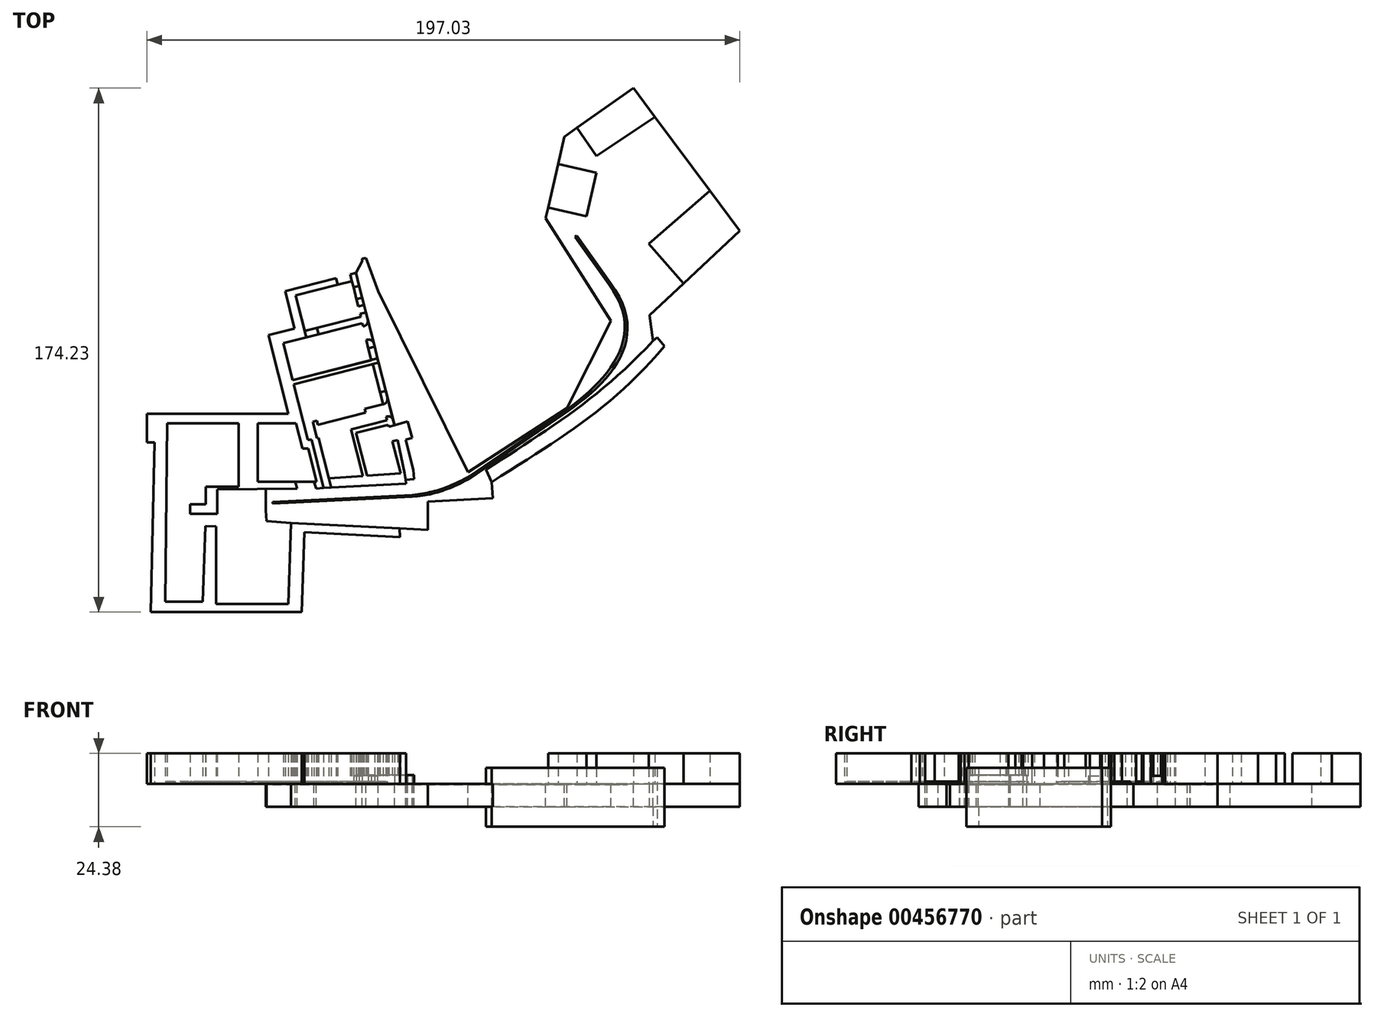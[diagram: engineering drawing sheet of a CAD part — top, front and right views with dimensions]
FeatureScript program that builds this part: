
annotation { "Feature Type Name" : "Feature", "Feature Type Description" : "" }
export const myFeature = defineFeature(function(context is Context, id is Id, definition is map)
    precondition{}
    {
        {
            var Q0;
            Q0=qCreatedBy(makeId("Top.planeOp"),FACE);
            var sketch = newSketch(context, id + "F0", { "sketchPlane" : qUnion([Q0])});
            skLineSegment(sketch, "E0", {"start": v(-16.8, 59.4) * mm, "end": v(-12.68, 48.38) * mm});
            skLineSegment(sketch, "E1", {"start": v(-12.68, 48.38) * mm, "end": v(17.13, -11.76) * mm});
            skLineSegment(sketch, "E2", {"start": v(17.13, -11.76) * mm, "end": v(50, 9.46) * mm});
            skLineSegment(sketch, "E3", {"start": v(50, 9.46) * mm, "end": v(64.66, 38.46) * mm});
            skLineSegment(sketch, "E4", {"start": v(64.66, 38.46) * mm, "end": v(42.95, 72.6) * mm});
            skLineSegment(sketch, "E5", {"start": v(50.27, 9.14) * mm, "end": v(17.8, -13.14) * mm});
            skLineSegment(sketch, "E6", {"start": v(-1.42, -19.38) * mm, "end": v(-47.79, -21.76) * mm});
            skLineSegment(sketch, "E7", {"start": v(-33.32, -17.22) * mm, "end": v(-3.46, -15.64) * mm});
            skLineSegment(sketch, "E8", {"start": v(-3.46, -15.64) * mm, "end": v(-3.54, -14.3) * mm});
            skLineSegment(sketch, "E9", {"start": v(-3.54, -14.3) * mm, "end": v(-0.76, -14.12) * mm});
            skLineSegment(sketch, "E10", {"start": v(-0.76, -14.12) * mm, "end": v(-0.95, -11.07) * mm});
            skLineSegment(sketch, "E11", {"start": v(-0.95, -11.07) * mm, "end": v(-3.53, -0.98) * mm});
            skLineSegment(sketch, "E12", {"start": v(-3.53, -0.98) * mm, "end": v(-1.33, -0.41) * mm});
            skLineSegment(sketch, "E13", {"start": v(-1.33, -0.41) * mm, "end": v(-2.86, 5.03) * mm});
            skLineSegment(sketch, "E14", {"start": v(-2.86, 5.03) * mm, "end": v(-7.26, 3.75) * mm});
            skLineSegment(sketch, "E15", {"start": v(-7.26, 3.75) * mm, "end": v(-20.08, 54.46) * mm});
            skFitSpline(sketch, "E16", {"points": [v(63.94, 50.75) * mm, v(50.27, 9.14) * mm], "startDerivative": vector(38.1, -51.9) * mm, "endDerivative": vector(-42.14, -31.36) * mm});
            skFitSpline(sketch, "E17", {"points": [v(17.8, -13.14) * mm, v(-1.42, -19.38) * mm], "startDerivative": vector(-22.13, -11.78) * mm, "endDerivative": vector(-20.75, -1.85) * mm});
            skLineSegment(sketch, "E18", {"start": v(-33.32, -17.22) * mm, "end": v(-34.01, -14.95) * mm});
            skLineSegment(sketch, "E19", {"start": v(-34.01, -14.95) * mm, "end": v(-40.26, -14.95) * mm});
            skLineSegment(sketch, "E20", {"start": v(-40.26, -14.95) * mm, "end": v(-39.68, -17.22) * mm});
            skLineSegment(sketch, "E21", {"start": v(-16.8, 59.4) * mm, "end": v(-18.08, 59.2) * mm});
            skLineSegment(sketch, "E22", {"start": v(-18.08, 59.2) * mm, "end": v(-18.08, 58.33) * mm});
            skLineSegment(sketch, "E23", {"start": v(-18.08, 58.33) * mm, "end": v(-20.08, 54.46) * mm});
            skLineSegment(sketch, "E24", {"start": v(-19.5, 52.18) * mm, "end": v(-40.07, 46.98) * mm});
            skLineSegment(sketch, "E25", {"start": v(-40.07, 46.98) * mm, "end": v(-37.07, 35.13) * mm});
            skLineSegment(sketch, "E26", {"start": v(-37.07, 35.13) * mm, "end": v(-18.4, 39.85) * mm});
            skLineSegment(sketch, "E27", {"start": v(-18.4, 39.85) * mm, "end": v(-18.65, 40.83) * mm});
            skLineSegment(sketch, "E28", {"start": v(-18.65, 40.83) * mm, "end": v(-16.76, 41.3) * mm});
            skLineSegment(sketch, "E29", {"start": v(-17.38, 43.77) * mm, "end": v(-19.28, 43.29) * mm});
            skLineSegment(sketch, "E30", {"start": v(-19.28, 43.29) * mm, "end": v(-21.4, 51.7) * mm});
            skLineSegment(sketch, "E31", {"start": v(-20.88, 49.63) * mm, "end": v(-18.98, 50.11) * mm});
            skLineSegment(sketch, "E32", {"start": v(-19.9, 45.75) * mm, "end": v(-18, 46.22) * mm});
            skLineSegment(sketch, "E33", {"start": v(-17.7, 36.65) * mm, "end": v(-17.98, 37.72) * mm});
            skLineSegment(sketch, "E34", {"start": v(-17.98, 37.72) * mm, "end": v(-44.24, 31.08) * mm});
            skLineSegment(sketch, "E35", {"start": v(-44.24, 31.08) * mm, "end": v(-41.14, 18.82) * mm});
            skLineSegment(sketch, "E36", {"start": v(-41.14, 18.82) * mm, "end": v(-14.94, 25.45) * mm});
            skLineSegment(sketch, "E37", {"start": v(-14.94, 25.45) * mm, "end": v(-16.63, 32.14) * mm});
            skLineSegment(sketch, "E38", {"start": v(-15.93, 29.39) * mm, "end": v(-13.87, 29.9) * mm});
            skLineSegment(sketch, "E39", {"start": v(-14.94, 25.45) * mm, "end": v(-12.88, 25.97) * mm});
            skLineSegment(sketch, "E40", {"start": v(-41.14, 18.82) * mm, "end": v(-40.78, 17.42) * mm});
            skLineSegment(sketch, "E41", {"start": v(-40.78, 17.42) * mm, "end": v(-12.52, 24.57) * mm});
            skLineSegment(sketch, "E42", {"start": v(-12.52, 24.57) * mm, "end": v(-14.44, 24.09) * mm});
            skLineSegment(sketch, "E43", {"start": v(-14.44, 24.09) * mm, "end": v(-9.72, 5.42) * mm});
            skLineSegment(sketch, "E44", {"start": v(-9.72, 5.42) * mm, "end": v(-33.02, -0.47) * mm});
            skLineSegment(sketch, "E45", {"start": v(-33.02, -0.47) * mm, "end": v(-34.4, 4.99) * mm});
            skLineSegment(sketch, "E46", {"start": v(-32.46, -0.33) * mm, "end": v(-29.05, -13.83) * mm});
            skLineSegment(sketch, "E47", {"start": v(-29.05, -13.83) * mm, "end": v(-17.78, -13.1) * mm});
            skLineSegment(sketch, "E48", {"start": v(-17.78, -13.1) * mm, "end": v(-21.7, 2.4) * mm});
            skLineSegment(sketch, "E49", {"start": v(-17.78, -13.1) * mm, "end": v(-5.26, -12.23) * mm});
            skLineSegment(sketch, "E50", {"start": v(-5.26, -12.23) * mm, "end": v(-9.33, 3.9) * mm});
            skLineSegment(sketch, "E51", {"start": v(-9.33, 3.9) * mm, "end": v(-20, 1.2) * mm});
            skLineSegment(sketch, "E52", {"start": v(-20, 1.2) * mm, "end": v(-16.41, -13) * mm});
            skFitSpline(sketch, "E53", {"points": [v(-11.07, 10.75) * mm, v(-9.76, 13.62) * mm], "startDerivative": vector(3.6, 0.68) * mm, "endDerivative": vector(-1.24, 4.91) * mm});
            skFitSpline(sketch, "E54", {"points": [v(-10.03, 6.63) * mm, v(-7.68, 5.42) * mm], "startDerivative": vector(2.9, 1.28) * mm, "endDerivative": vector(0.82, -3.25) * mm});
            skFitSpline(sketch, "E55", {"points": [v(-17.7, 36.65) * mm, v(-16.28, 39.4) * mm], "startDerivative": vector(2.72, 0.7) * mm, "endDerivative": vector(-1.58, 6.25) * mm});
            skFitSpline(sketch, "E56", {"points": [v(-16.63, 32.14) * mm, v(-14.15, 31) * mm], "startDerivative": vector(3.6, 1.24) * mm, "endDerivative": vector(0.77, -3.05) * mm});
            skLineSegment(sketch, "E57", {"start": v(-34.4, 4.99) * mm, "end": v(-33.07, 5.32) * mm});
            skLineSegment(sketch, "E58", {"start": v(-33.07, 5.32) * mm, "end": v(-32.74, 4) * mm});
            skLineSegment(sketch, "E59", {"start": v(-32.74, 4) * mm, "end": v(-16.88, 8) * mm});
            skLineSegment(sketch, "E60", {"start": v(-16.88, 8) * mm, "end": v(-17.18, 9.2) * mm});
            skLineSegment(sketch, "E61", {"start": v(-17.18, 9.2) * mm, "end": v(-11.07, 10.75) * mm});
            skLineSegment(sketch, "E62", {"start": v(-3.97, -12.12) * mm, "end": v(-5.26, -12.23) * mm});
            skLineSegment(sketch, "E63", {"start": v(-7.26, 3.75) * mm, "end": v(-9.17, 3.27) * mm});
            skLineSegment(sketch, "E64", {"start": v(-40.78, 17.42) * mm, "end": v(-36.1, -1.06) * mm});
            skLineSegment(sketch, "E65", {"start": v(-36.1, -1.06) * mm, "end": v(-34.85, -1.06) * mm});
            skLineSegment(sketch, "E66", {"start": v(-34.85, -1.06) * mm, "end": v(-30.77, -17.22) * mm});
            skLineSegment(sketch, "E67", {"start": v(-37.07, 35.13) * mm, "end": v(-36.54, 33.03) * mm});
            skLineSegment(sketch, "E68", {"start": v(-33.07, 36.14) * mm, "end": v(-32.54, 34.04) * mm});
            skLineSegment(sketch, "E69", {"start": v(-52.76, 4.4) * mm, "end": v(-39.99, 4.4) * mm});
            skLineSegment(sketch, "E70", {"start": v(-39.99, 4.4) * mm, "end": v(-37.89, -3.9) * mm});
            skLineSegment(sketch, "E71", {"start": v(-37.89, -3.9) * mm, "end": v(-35.98, -3.9) * mm});
            skLineSegment(sketch, "E72", {"start": v(-35.98, -3.9) * mm, "end": v(-33.2, -14.94) * mm});
            skLineSegment(sketch, "E73", {"start": v(-33.2, -14.94) * mm, "end": v(-34.01, -14.95) * mm});
            skLineSegment(sketch, "E74", {"start": v(-40.26, -14.95) * mm, "end": v(-52.66, -14.95) * mm});
            skLineSegment(sketch, "E75", {"start": v(-52.66, -14.95) * mm, "end": v(-52.76, 4.4) * mm});
            skLineSegment(sketch, "E76", {"start": v(-20.08, 54.46) * mm, "end": v(-21.93, 54) * mm});
            skLineSegment(sketch, "E77", {"start": v(-21.93, 54) * mm, "end": v(-21.4, 51.7) * mm});
            skLineSegment(sketch, "E78", {"start": v(-26.16, 50.5) * mm, "end": v(-26.71, 52.66) * mm});
            skLineSegment(sketch, "E79", {"start": v(-26.71, 52.66) * mm, "end": v(-43.6, 48.39) * mm});
            skLineSegment(sketch, "E80", {"start": v(-43.6, 48.39) * mm, "end": v(-40.45, 35.96) * mm});
            skLineSegment(sketch, "E81", {"start": v(-40.45, 35.96) * mm, "end": v(-49.2, 33.75) * mm});
            skLineSegment(sketch, "E82", {"start": v(-49.2, 33.75) * mm, "end": v(-42.59, 7.59) * mm});
            skLineSegment(sketch, "E83", {"start": v(-42.59, 7.59) * mm, "end": v(-89.55, 7.59) * mm});
            skLineSegment(sketch, "E84", {"start": v(-89.55, 7.59) * mm, "end": v(-89.55, -1.93) * mm});
            skLineSegment(sketch, "E85", {"start": v(-89.55, -1.93) * mm, "end": v(-87.02, -1.93) * mm});
            skLineSegment(sketch, "E86", {"start": v(-87.02, -1.93) * mm, "end": v(-88.24, -58.34) * mm});
            skLineSegment(sketch, "E87", {"start": v(-88.24, -58.34) * mm, "end": v(-38.09, -58.34) * mm});
            skLineSegment(sketch, "E88", {"start": v(-38.09, -58.34) * mm, "end": v(-37.15, -31.78) * mm});
            skLineSegment(sketch, "E89", {"start": v(-37.15, -31.78) * mm, "end": v(-5.4, -33.34) * mm});
            skLineSegment(sketch, "E90", {"start": v(-5.62, -30.5) * mm, "end": v(-41.63, -28.73) * mm});
            skLineSegment(sketch, "E91", {"start": v(-41.63, -28.73) * mm, "end": v(-42.58, -55.6) * mm});
            skLineSegment(sketch, "E92", {"start": v(-42.58, -55.6) * mm, "end": v(-66.55, -55.6) * mm});
            skLineSegment(sketch, "E93", {"start": v(-66.55, -55.6) * mm, "end": v(-66.55, -29.8) * mm});
            skLineSegment(sketch, "E94", {"start": v(-66.55, -29.8) * mm, "end": v(-70.14, -29.68) * mm});
            skLineSegment(sketch, "E95", {"start": v(-70.14, -29.68) * mm, "end": v(-71.03, -54.86) * mm});
            skLineSegment(sketch, "E96", {"start": v(-71.03, -54.86) * mm, "end": v(-83.38, -54.86) * mm});
            skLineSegment(sketch, "E97", {"start": v(-83.38, -54.86) * mm, "end": v(-82.83, 4.49) * mm});
            skLineSegment(sketch, "E98", {"start": v(-82.83, 4.49) * mm, "end": v(-59.06, 4.49) * mm});
            skLineSegment(sketch, "E99", {"start": v(-59.06, 4.49) * mm, "end": v(-59.06, -16.63) * mm});
            skLineSegment(sketch, "E100", {"start": v(-59.06, -16.63) * mm, "end": v(-69.91, -16.63) * mm});
            skLineSegment(sketch, "E101", {"start": v(-69.91, -16.63) * mm, "end": v(-69.91, -22.47) * mm});
            skLineSegment(sketch, "E102", {"start": v(-69.91, -22.47) * mm, "end": v(-75.2, -22.47) * mm});
            skLineSegment(sketch, "E103", {"start": v(-75.2, -22.47) * mm, "end": v(-75.2, -25.64) * mm});
            skLineSegment(sketch, "E104", {"start": v(-75.2, -25.64) * mm, "end": v(-66.12, -25.64) * mm});
            skLineSegment(sketch, "E105", {"start": v(-66.12, -25.64) * mm, "end": v(-66.12, -17.56) * mm});
            skLineSegment(sketch, "E106", {"start": v(-66.12, -17.56) * mm, "end": v(-39.68, -17.22) * mm});
            skLineSegment(sketch, "E107", {"start": v(18.09, -13.67) * mm, "end": v(50.57, 8.68) * mm});
            skFitSpline(sketch, "E108", {"points": [v(64.52, 51.04) * mm, v(50.57, 8.68) * mm], "startDerivative": vector(39.56, -52.78) * mm, "endDerivative": vector(-44.9, -31.32) * mm});
            skLineSegment(sketch, "E109", {"start": v(77.5, 40.4) * mm, "end": v(78.58, 31.84) * mm});
            skLineSegment(sketch, "E110", {"start": v(-47.79, -21.76) * mm, "end": v(-47.79, -22.27) * mm});
            skLineSegment(sketch, "E111", {"start": v(110.36, 67.84) * mm, "end": v(78.8, 40.04) * mm});
            skLineSegment(sketch, "E112", {"start": v(78.8, 40.04) * mm, "end": v(79.97, 32.97) * mm});
            skLineSegment(sketch, "E113", {"start": v(79.97, 32.97) * mm, "end": v(78.58, 31.84) * mm});
            skFitSpline(sketch, "E114", {"points": [v(78.58, 31.84) * mm, v(23.06, -10.96) * mm], "startDerivative": vector(-52.96, -57.58) * mm, "endDerivative": vector(-59.2, -38.23) * mm});
            skFitSpline(sketch, "E115", {"points": [v(24.98, -15.08) * mm, v(82.37, 30.03) * mm], "startDerivative": vector(71.51, 45.24) * mm, "endDerivative": vector(51.78, 61.27) * mm});
            skLineSegment(sketch, "E116", {"start": v(79.97, 32.97) * mm, "end": v(82.37, 30.03) * mm});
            skLineSegment(sketch, "E117", {"start": v(23.06, -10.96) * mm, "end": v(24.98, -15.08) * mm});
            skLineSegment(sketch, "E118", {"start": v(24.98, -15.08) * mm, "end": v(25.38, -20.49) * mm});
            skLineSegment(sketch, "E119", {"start": v(25.38, -20.49) * mm, "end": v(-49.98, -24.49) * mm});
            skLineSegment(sketch, "E120", {"start": v(-49.98, -24.49) * mm, "end": v(-50.07, -17.35) * mm});
            skLineSegment(sketch, "E121", {"start": v(-49.98, -24.49) * mm, "end": v(-49.79, -28.13) * mm});
            skLineSegment(sketch, "E122", {"start": v(-49.79, -28.13) * mm, "end": v(-41.63, -28.73) * mm});
            skLineSegment(sketch, "E123", {"start": v(-41.63, -28.73) * mm, "end": v(3.83, -30.97) * mm});
            skLineSegment(sketch, "E124", {"start": v(3.83, -30.97) * mm, "end": v(3.83, -21.63) * mm});
            skLineSegment(sketch, "E125", {"start": v(-5.62, -30.5) * mm, "end": v(-5.4, -33.34) * mm});
            skLineSegment(sketch, "E126", {"start": v(-3.97, -12.12) * mm, "end": v(-3.54, -14.3) * mm});
            skLineSegment(sketch, "E127", {"start": v(-7.26, 3.75) * mm, "end": v(-3.97, -12.12) * mm});
            skLineSegment(sketch, "E128", {"start": v(-7.96, -1.54) * mm, "end": v(-6.25, -1.11) * mm});
            skLineSegment(sketch, "E129", {"start": v(-6.25, -1.11) * mm, "end": v(-3.53, -0.98) * mm});
            skLineSegment(sketch, "E130", {"start": v(-0.95, -11.07) * mm, "end": v(-3.97, -12.12) * mm});
            skLineSegment(sketch, "E131", {"start": v(-13.5, 20.38) * mm, "end": v(-11.59, 20.87) * mm});
            skLineSegment(sketch, "E132", {"start": v(-12.08, 14.75) * mm, "end": v(-10.17, 15.24) * mm});
            skLineSegment(sketch, "E133", {"start": v(-29.05, -13.83) * mm, "end": v(-28.26, -16.95) * mm});
            skLineSegment(sketch, "E134", {"start": v(42.95, 72.6) * mm, "end": v(49.14, 99.73) * mm});
            skLineSegment(sketch, "E135", {"start": v(49.14, 99.73) * mm, "end": v(72.16, 115.89) * mm});
            skLineSegment(sketch, "E136", {"start": v(72.16, 115.89) * mm, "end": v(107.48, 68.41) * mm});
            skLineSegment(sketch, "E137", {"start": v(107.48, 68.41) * mm, "end": v(77.5, 40.4) * mm});
            skLineSegment(sketch, "E138", {"start": v(97.5, 81.82) * mm, "end": v(77.27, 64.14) * mm});
            skLineSegment(sketch, "E139", {"start": v(77.27, 64.14) * mm, "end": v(88.8, 50.95) * mm});
            skLineSegment(sketch, "E140", {"start": v(110.36, 67.84) * mm, "end": v(71.93, 119.48) * mm});
            skLineSegment(sketch, "E141", {"start": v(71.93, 119.48) * mm, "end": v(60.82, 111.21) * mm});
            skLineSegment(sketch, "E142", {"start": v(60.82, 111.21) * mm, "end": v(62.36, 109.01) * mm});
            skLineSegment(sketch, "E143", {"start": v(59.78, 93.3) * mm, "end": v(79.26, 106.35) * mm});
            skLineSegment(sketch, "E144", {"start": v(53.34, 102.68) * mm, "end": v(59.78, 93.3) * mm});
            skLineSegment(sketch, "E145", {"start": v(47.08, 90.7) * mm, "end": v(59.78, 87.8) * mm});
            skLineSegment(sketch, "E146", {"start": v(59.78, 87.8) * mm, "end": v(56.47, 73.3) * mm});
            skLineSegment(sketch, "E147", {"start": v(56.47, 73.3) * mm, "end": v(43.77, 76.19) * mm});
            skLineSegment(sketch, "E148", {"start": v(-47.79, -22.27) * mm, "end": v(-1.38, -19.92) * mm});
            skFitSpline(sketch, "E149", {"points": [v(-1.38, -19.92) * mm, v(18.09, -13.67) * mm], "startDerivative": vector(20.68, 1.3) * mm, "endDerivative": vector(21.88, 12.06) * mm});
            skLineSegment(sketch, "E150", {"start": v(63.94, 50.75) * mm, "end": v(52.75, 66.42) * mm});
            skLineSegment(sketch, "E151", {"start": v(52.75, 66.42) * mm, "end": v(53.36, 66.86) * mm});
            skLineSegment(sketch, "E152", {"start": v(53.36, 66.86) * mm, "end": v(64.52, 51.04) * mm});
            skSolve(sketch);
        }
        {
            var Q0;
            Q0=makeQuery(id+"F0.imprint","IMPRINT",FACE,{"disambiguationData":[TD([[makeQuery(id+"F0.imprint","IMPRINT",EDGE,{"derivedFrom":sQuery(id+"F0.wireOp",EDGE,"E5")}),1.0]])]});
            var Q1;
            {var subQ0=sQuery(id+"F0.wireOp",EDGE,"E145");Q1=makeQuery(id+"F0.imprint","IMPRINT",FACE,{"disambiguationData":[TD([[makeQuery(id+"F0.imprint","IMPRINT",EDGE,{"derivedFrom":subQ0}),-1.0]])]});}
            var Q2;
            {var subQ0=sQuery(id+"F0.wireOp",EDGE,"E143");Q2=makeQuery(id+"F0.imprint","IMPRINT",FACE,{"disambiguationData":[TD([[makeQuery(id+"F0.imprint","IMPRINT",EDGE,{"derivedFrom":subQ0}),1.0]])]});}
            var Q3;
            {var subQ3=sQuery(id+"F0.wireOp",EDGE,"E138");Q3=makeQuery(id+"F0.imprint","IMPRINT",FACE,{"disambiguationData":[TD([[makeQuery(id+"F0.imprint","IMPRINT",EDGE,{"derivedFrom":subQ3}),1.0]])]});}
            var Q4;
            {var subQ3=sQuery(id+"F0.wireOp",EDGE,"E121");Q4=makeQuery(id+"F0.imprint","IMPRINT",FACE,{"disambiguationData":[TD([[makeQuery(id+"F0.imprint","IMPRINT",EDGE,{"derivedFrom":subQ3}),1.0]])]});}
            var Q5;
            Q5=makeQuery(id+"F0.imprint","IMPRINT",FACE,{"disambiguationData":[TD([[makeQuery(id+"F0.imprint","IMPRINT",EDGE,{"derivedFrom":sQuery(id+"F0.wireOp",EDGE,"E0")}),-1.0]])]});
            extrude(context, id + "F1", {"entities" : qUnion([Q0, Q1, Q2, Q3, Q4, Q5]), "oppositeDirection" : true, "depth" : 7.62 * mm});
        }
        {
            var Q0;
            Q0=makeQuery(id+"F0.imprint","IMPRINT",FACE,{"disambiguationData":[TD([[makeQuery(id+"F0.imprint","IMPRINT",EDGE,{"derivedFrom":sQuery(id+"F0.wireOp",EDGE,"E5")}),1.0]])]});
            extrude(context, id + "F2", {"entities" : qUnion([Q0]), "operationType" : NewBodyOperationType.REMOVE, "oppositeDirection" : true, "depth" : 0.25 * mm});
        }
        {
            var Q0;
            {var subQ0=sQuery(id+"F0.wireOp",EDGE,"E131");Q0=makeQuery(id+"F0.imprint","IMPRINT",FACE,{"disambiguationData":[TD([[makeQuery(id+"F0.imprint","IMPRINT",EDGE,{"derivedFrom":subQ0}),-1.0]])]});}
            var Q1;
            {var subQ12=sQuery(id+"F0.wireOp",EDGE,"E41");Q1=makeQuery(id+"F0.imprint","IMPRINT",FACE,{"disambiguationData":[TD([[makeQuery(id+"F0.imprint","IMPRINT",EDGE,{"derivedFrom":subQ12}),-1.0]])]});}
            var Q2;
            {var subQ9=sQuery(id+"F0.wireOp",EDGE,"E33");Q2=makeQuery(id+"F0.imprint","IMPRINT",FACE,{"disambiguationData":[TD([[makeQuery(id+"F0.imprint","IMPRINT",EDGE,{"derivedFrom":subQ9}),1.0]])]});}
            var Q3;
            {var subQ5=sQuery(id+"F0.wireOp",EDGE,"E25");Q3=makeQuery(id+"F0.imprint","IMPRINT",FACE,{"disambiguationData":[TD([[makeQuery(id+"F0.imprint","IMPRINT",EDGE,{"derivedFrom":subQ5}),1.0]])]});}
            extrude(context, id + "F3", {"entities" : qUnion([Q0, Q1, Q2, Q3]), "depth" : 0.76 * mm});
        }
        {
            var Q0;
            {var subQ0=sQuery(id+"F0.wireOp",EDGE,"E48");Q0=makeQuery(id+"F0.imprint","IMPRINT",FACE,{"disambiguationData":[TD([[makeQuery(id+"F0.imprint","IMPRINT",EDGE,{"derivedFrom":subQ0}),-1.0]])]});}
            var Q1;
            {var subQ0=sQuery(id+"F0.wireOp",EDGE,"E53");Q1=makeQuery(id+"F0.imprint","IMPRINT",FACE,{"disambiguationData":[TD([[makeQuery(id+"F0.imprint","IMPRINT",EDGE,{"derivedFrom":subQ0}),1.0]])]});}
            var Q2;
            {var subQ0=sQuery(id+"F0.wireOp",EDGE,"E42");Q2=makeQuery(id+"F0.imprint","IMPRINT",FACE,{"disambiguationData":[TD([[makeQuery(id+"F0.imprint","IMPRINT",EDGE,{"derivedFrom":subQ0}),1.0]])]});}
            var Q3;
            {var subQ0=sQuery(id+"F0.wireOp",EDGE,"E38");Q3=makeQuery(id+"F0.imprint","IMPRINT",FACE,{"disambiguationData":[TD([[makeQuery(id+"F0.imprint","IMPRINT",EDGE,{"derivedFrom":subQ0}),1.0]])]});}
            var Q4;
            Q4=makeQuery(id+"F0.imprint","IMPRINT",FACE,{"disambiguationData":[TD([[makeQuery(id+"F0.imprint","IMPRINT",EDGE,{"derivedFrom":sQuery(id+"F0.wireOp",EDGE,"E36")}),-1.0]])]});
            var Q5;
            {var subQ1=sQuery(id+"F0.wireOp",EDGE,"E27");Q5=makeQuery(id+"F0.imprint","IMPRINT",FACE,{"disambiguationData":[TD([[makeQuery(id+"F0.imprint","IMPRINT",EDGE,{"derivedFrom":subQ1}),-1.0]])]});}
            var Q6;
            {var subQ1=sQuery(id+"F0.wireOp",EDGE,"E18");Q6=makeQuery(id+"F0.imprint","IMPRINT",FACE,{"disambiguationData":[TD([[makeQuery(id+"F0.imprint","IMPRINT",EDGE,{"derivedFrom":subQ1}),-1.0]])]});}
            var Q7;
            {var subQ0=sQuery(id+"F0.wireOp",EDGE,"E29");Q7=makeQuery(id+"F0.imprint","IMPRINT",FACE,{"disambiguationData":[TD([[makeQuery(id+"F0.imprint","IMPRINT",EDGE,{"derivedFrom":subQ0}),-1.0]])]});}
            var Q8;
            {var subQ0=sQuery(id+"F0.wireOp",EDGE,"E76");Q8=makeQuery(id+"F0.imprint","IMPRINT",FACE,{"disambiguationData":[TD([[makeQuery(id+"F0.imprint","IMPRINT",EDGE,{"derivedFrom":subQ0}),1.0]])]});}
            var Q9;
            {var subQ3=sQuery(id+"F0.wireOp",EDGE,"E31");Q9=makeQuery(id+"F0.imprint","IMPRINT",FACE,{"disambiguationData":[TD([[makeQuery(id+"F0.imprint","IMPRINT",EDGE,{"derivedFrom":subQ3}),1.0]])]});}
            var Q10;
            {var subQ0=sQuery(id+"F0.wireOp",EDGE,"E62");Q10=makeQuery(id+"F0.imprint","IMPRINT",FACE,{"disambiguationData":[TD([[makeQuery(id+"F0.imprint","IMPRINT",EDGE,{"derivedFrom":subQ0}),-1.0]])]});}
            var Q11;
            {var subQ1=sQuery(id+"F0.wireOp",EDGE,"E8");Q11=makeQuery(id+"F0.imprint","IMPRINT",FACE,{"disambiguationData":[TD([[makeQuery(id+"F0.imprint","IMPRINT",EDGE,{"derivedFrom":subQ1}),1.0]])]});}
            var Q12;
            {var subQ0=sQuery(id+"F0.wireOp",EDGE,"E145");Q12=makeQuery(id+"F0.imprint","IMPRINT",FACE,{"disambiguationData":[TD([[makeQuery(id+"F0.imprint","IMPRINT",EDGE,{"derivedFrom":subQ0}),-1.0]])]});}
            var Q13;
            {var subQ0=sQuery(id+"F0.wireOp",EDGE,"E143");Q13=makeQuery(id+"F0.imprint","IMPRINT",FACE,{"disambiguationData":[TD([[makeQuery(id+"F0.imprint","IMPRINT",EDGE,{"derivedFrom":subQ0}),1.0]])]});}
            var Q14;
            {var subQ3=sQuery(id+"F0.wireOp",EDGE,"E138");Q14=makeQuery(id+"F0.imprint","IMPRINT",FACE,{"disambiguationData":[TD([[makeQuery(id+"F0.imprint","IMPRINT",EDGE,{"derivedFrom":subQ3}),1.0]])]});}
            extrude(context, id + "F4", {"entities" : qUnion([Q0, Q1, Q2, Q3, Q4, Q5, Q6, Q7, Q8, Q9, Q10, Q11, Q12, Q13, Q14]), "depth" : 10.16 * mm});
        }
        {
            var Q0;
            Q0=makeQuery(id+"F0.imprint","IMPRINT",FACE,{"disambiguationData":[TD([[makeQuery(id+"F0.imprint","IMPRINT",EDGE,{"derivedFrom":sQuery(id+"F0.wireOp",EDGE,"E91")}),-1.0]])]});
            var Q1;
            Q1=makeQuery(id+"F0.imprint","IMPRINT",FACE,{"disambiguationData":[TD([[makeQuery(id+"F0.imprint","IMPRINT",EDGE,{"derivedFrom":sQuery(id+"F0.wireOp",EDGE,"E19")}),-1.0]])]});
            extrude(context, id + "F5", {"entities" : qUnion([Q0, Q1]), "operationType" : NewBodyOperationType.ADD, "depth" : 0.76 * mm});
        }
        {
            var Q0;
            {var subQ0=sQuery(id+"F0.wireOp",EDGE,"E45");Q0=makeQuery(id+"F0.imprint","IMPRINT",FACE,{"disambiguationData":[TD([[makeQuery(id+"F0.imprint","IMPRINT",EDGE,{"derivedFrom":subQ0}),-1.0]])]});}
            var Q1;
            {var subQ0=sQuery(id+"F0.wireOp",EDGE,"E46");Q1=makeQuery(id+"F0.imprint","IMPRINT",FACE,{"disambiguationData":[TD([[makeQuery(id+"F0.imprint","IMPRINT",EDGE,{"derivedFrom":subQ0}),1.0]])]});}
            var Q2;
            {var subQ0=sQuery(id+"F0.wireOp",EDGE,"E53");Q2=makeQuery(id+"F0.imprint","IMPRINT",FACE,{"disambiguationData":[TD([[makeQuery(id+"F0.imprint","IMPRINT",EDGE,{"derivedFrom":subQ0}),-1.0]])]});}
            extrude(context, id + "F6", {"entities" : qUnion([Q0, Q1, Q2]), "oppositeDirection" : true, "depth" : 0.25 * mm});
        }
        {
            var Q0;
            {var subQ0=sQuery(id+"F0.wireOp",EDGE,"E38");Q0=makeQuery(id+"F0.imprint","IMPRINT",FACE,{"disambiguationData":[TD([[makeQuery(id+"F0.imprint","IMPRINT",EDGE,{"derivedFrom":subQ0}),-1.0]])]});}
            var Q1;
            {var subQ0=sQuery(id+"F0.wireOp",EDGE,"E31");Q1=makeQuery(id+"F0.imprint","IMPRINT",FACE,{"disambiguationData":[TD([[makeQuery(id+"F0.imprint","IMPRINT",EDGE,{"derivedFrom":subQ0}),-1.0]])]});}
            extrude(context, id + "F7", {"entities" : qUnion([Q0, Q1]), "depth" : 2.77 * mm});
        }
        {
            var Q0;
            Q0=makeQuery(id+"F0.imprint","IMPRINT",FACE,{"disambiguationData":[TD([[makeQuery(id+"F0.imprint","IMPRINT",EDGE,{"derivedFrom":sQuery(id+"F0.wireOp",EDGE,"E113")}),1.0]])]});
            extrude(context, id + "F8", {"entities" : qUnion([Q0]), "operationType" : NewBodyOperationType.ADD, "depth" : 5.33 * mm, "hasSecondDirection" : true, "secondDirectionOppositeDirection" : true, "secondDirectionDepth" : 14.22 * mm});
        }
        {
            var Q0;
            Q0=makeQuery(id+"F0.imprint","IMPRINT",FACE,{"disambiguationData":[TD([[makeQuery(id+"F0.imprint","IMPRINT",EDGE,{"derivedFrom":sQuery(id+"F0.wireOp",EDGE,"E12")}),1.0]])]});
            var Q1;
            Q1=makeQuery(id+"F0.imprint","IMPRINT",FACE,{"disambiguationData":[TD([[makeQuery(id+"F0.imprint","IMPRINT",EDGE,{"derivedFrom":sQuery(id+"F0.wireOp",EDGE,"E11")}),1.0]])]});
            var Q2;
            Q2=makeQuery(id+"F0.imprint","IMPRINT",FACE,{"disambiguationData":[TD([[makeQuery(id+"F0.imprint","IMPRINT",EDGE,{"derivedFrom":sQuery(id+"F0.wireOp",EDGE,"E9")}),1.0]])]});
            var Q3;
            {var subQ0=sQuery(id+"F0.wireOp",EDGE,"E63");Q3=makeQuery(id+"F0.imprint","IMPRINT",FACE,{"disambiguationData":[TD([[makeQuery(id+"F0.imprint","IMPRINT",EDGE,{"derivedFrom":subQ0}),1.0]])]});}
            var Q4;
            {var subQ0=sQuery(id+"F0.wireOp",EDGE,"E51");Q4=makeQuery(id+"F0.imprint","IMPRINT",FACE,{"disambiguationData":[TD([[makeQuery(id+"F0.imprint","IMPRINT",EDGE,{"derivedFrom":subQ0}),1.0]])]});}
            extrude(context, id + "F9", {"entities" : qUnion([Q0, Q1, Q2, Q3, Q4]), "operationType" : NewBodyOperationType.ADD, "depth" : 2.95 * mm});
        }
    });
